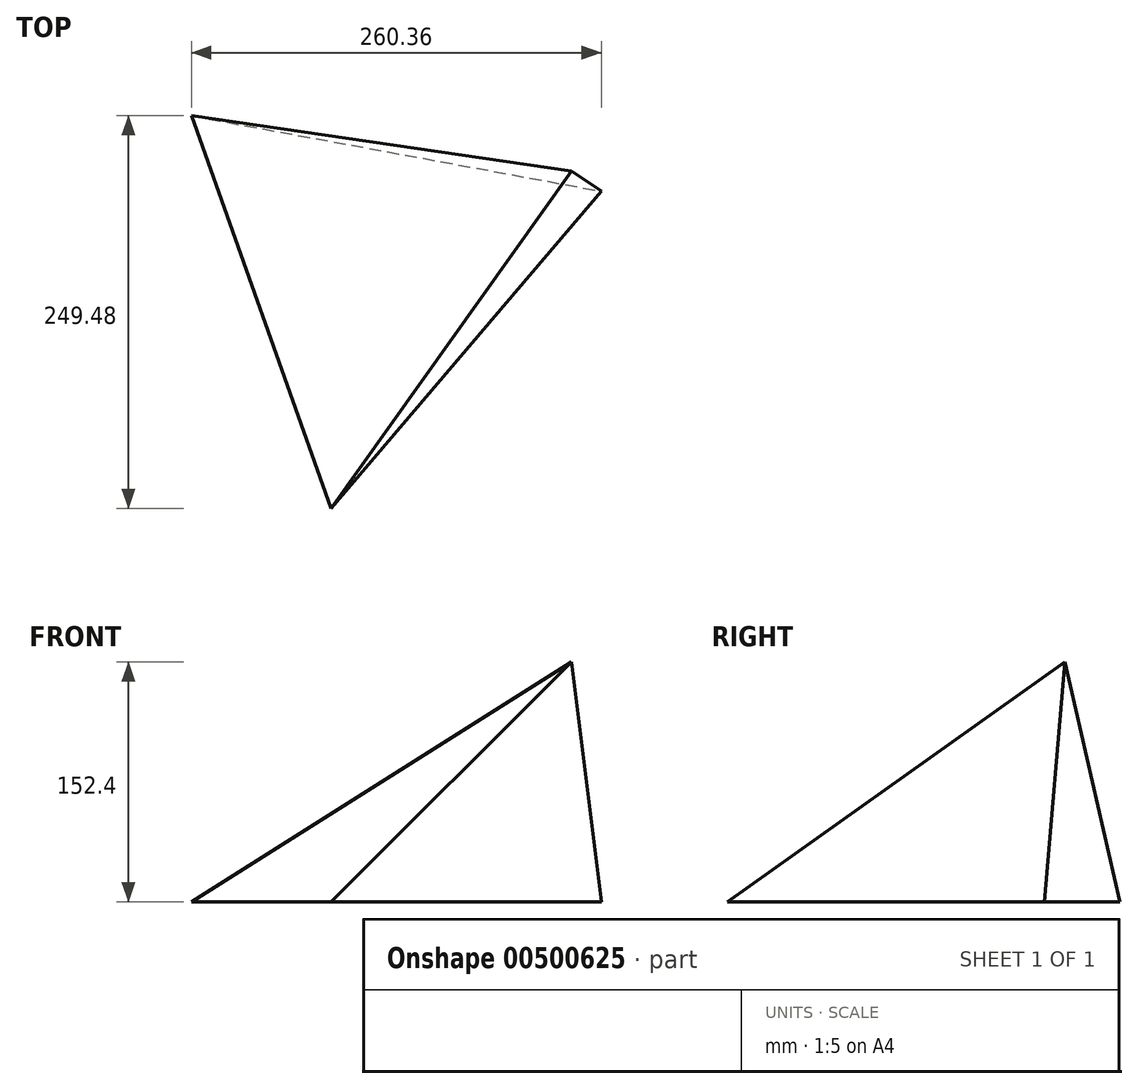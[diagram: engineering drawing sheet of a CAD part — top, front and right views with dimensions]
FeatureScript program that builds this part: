
annotation { "Feature Type Name" : "Feature", "Feature Type Description" : "" }
export const myFeature = defineFeature(function(context is Context, id is Id, definition is map)
    precondition{}
    {
        {
            var Q0;
            Q0=qCreatedBy(makeId("Top.planeOp"),FACE);
            var sketch = newSketch(context, id + "F0", { "sketchPlane" : qUnion([Q0])});
            skCircle(sketch, "E0.cCircle", {"center": v(0, 0) * mm, "radius": 152.85 * mm, "construction": true});
            skLineSegment(sketch, "E0.0", {"start": v(144.03, 51.16) * mm, "end": v(-27.7, -150.32) * mm});
            skLineSegment(sketch, "E0.1", {"start": v(-27.7, -150.32) * mm, "end": v(-116.33, 99.16) * mm});
            skLineSegment(sketch, "E0.2", {"start": v(-116.33, 99.16) * mm, "end": v(144.03, 51.16) * mm});
            skSolve(sketch);
        }
        {
            var Q0;
            Q0=makeQuery(id+"F0.imprint","IMPRINT",FACE,{"disambiguationData":[TD([[makeQuery(id+"F0.imprint","IMPRINT",EDGE,{"derivedFrom":sQuery(id+"F0.wireOp",EDGE,"E0.0")}),-1.0]])]});
            cPlane(context, id + "F1", {"entities" : qUnion([Q0]), "cplaneType" : CPlaneType.OFFSET, "offset" : 152.4 * mm, "width" : 152.4 * mm, "height" : 152.4 * mm});
        }
        {
            var Q0;
            Q0=qCreatedBy(id+"F1.planeOp",FACE);
            var sketch = newSketch(context, id + "F2", { "sketchPlane" : qUnion([Q0])});
            skPoint(sketch, "E1", {"position": v(125, 64.03) * mm});
            skSolve(sketch);
        }
        {
            var Q0;
            Q0=makeQuery(id+"F0.imprint","IMPRINT",FACE,{"disambiguationData":[TD([[makeQuery(id+"F0.imprint","IMPRINT",EDGE,{"derivedFrom":sQuery(id+"F0.wireOp",EDGE,"E0.0")}),-1.0]])]});
            var Q1;
            Q1=sQuery(id+"F2.wireOp",VERTEX,"E1");
            loft(context, id + "F3", {"sheetProfilesArray" : [{ "sheetProfileEntities" : qUnion([Q0]) }, { "sheetProfileEntities" : qUnion([Q1]) }]});
        }
    });
